# Revit family: KDW030073
name_source: partatom
category: Plumbing Fixtures
revit_build: Autodesk Revit 2015 (Build: 20140606_1530(x64)
units: mm (PartAtom-declared; Revit-internal decimal feet)

## types (1)
- KDW030073
    BIMobject category = Bath & Spas
    Brand url = http://www.kaldewei.com
    Color = https://www.kaldewei.co.uk
    ColourOptions = https://www.kaldewei.co.uk
    Description = KALDEWEI international Worldwide partner for iconic bathroom solutions made of KALDEWEI steel enamel KALDEWEI steel enamel delivers unique advantages that inspire excellence in bathroom design. Projects across the world, from upmarket hotels to private homes, capture the sophisticated aesthetic that recommends KALDEWEI as the partner of choice. As a leading international manufacturer of high-quality shower surfaces, bathtubs and washbasins made of superior steel enamel, KALDEWEI today is present in more than 80 countries.
    Design country = Germany
    DrainSize = 52 mm
    Durability = https://EN 14516
    Edition number = 1
    Features = https://www.kaldewei.co.uk
    Finish = https://www.kaldewei.co.uk
    Finition = Kaldewei
    HasGrabHandles = https://www.kaldewei.co.uk
    IFC Classification = Furnishing Element
    IfcExportAs = BATH
    IfcExportType = IfcSanitaryTerminalType
    IntegralAccessories = https://www.kaldewei.co.uk
    Manufacturer = KALDEWEI
    Manufacturer country = Germany
    ManufacturerCountry = GERMANY
    ManufacturerName = KALDEWEI
    Material = steel enamel
    Material main = Steel
    Material secondary = Enamel
    Model = Ellipso Duo Oval 1900x1000x465
    NBS Reference Code = 35-06-08
    NBS Reference Description = Baths
    Name = ELLIPSO DUO OVAL
    Nominal height = 1000 cm
    Nominal width = 1900 cm
    ObjectName = ELLIPSO DUO OVAL 1900x1000x465
    ObjectNorm = EN 14516 EU DECLARATION OF PERFORMANCE (https://www.kaldewei.de
    Polantis code = KDW030073
    Product Guid = 10a9a2e4-e12a-4da1-87b0-59279412799b
    Product SKU = 232
    Product certification = https://www.kaldewei.co.uk
    Product data url = http://bimobject.com
    Product family = ELLIPSO DUO
    Product group = Bathtub
    Product url = https://www.kaldewei.co.uk
    ProductInformation = Model No. 232: The soft, elliptical inner contour of ELLIPSO DUO OVAL promises a new sense of security and comfort. The rounded shoulder section and carefully calibrated side walls create a generous space in which to lean back and relax, either alone or with a partner.
    QR code = http://bimobject.com
    SerialNumber = 232
    Shape = Oval baths
    Size = 1900x1000x465
    Sound Insulation = DIN 4109:2016; VDI4100:2012
    SupportFrame = https://www.kaldewei.co.uk
    Sustainability = https://kaldewei-fa.secure.footprint.net
    Technical description = https://www.kaldewei.co.uk
    TechnicalDataURL = https://kaldewei.typo-live.web-factory.de
    Type Comments = Model No. 232: The soft, elliptical inner contour of ELLIPSO DUO OVAL promises a new sense of security and comfort. The rounded shoulder section and carefully calibrated side walls create a generous space in which to lean back and relax, either alone or with a partner.
    UNSPSC Code = 30181501
    UNSPSCCode = 30181500
    UNSPSCNames = Sanitary ware
    URL = https://www.kaldewei.com
    Uniclass 1.4 Code = L7211
    Uniclass 1.4 Description = Baths
    Uniclass 2.0 Code = PR-35-06-08
    Uniclass 2.0 Description = Baths
    Uniclass 2015 = Pr_40_20_06_08
    Version = 1
    VolumeToOverflowMaximum = 214
    WarrantyDurationParts = 30
    WarrantyDurationUnit = Year
    WarrantyStartDate = https://www.kaldewei.co.uk
    WaterSupplyOverflowAndWasteHolesOverflow = 52 mm
    WaterSupplyOverflowAndWasteHolesWaste = 52 mm
    Weight = 55
    Weight Net (Kg) = 55

## geometry (parser evidence)
native form markers: Sweep x6
no freeform markers — native parametric forms only
